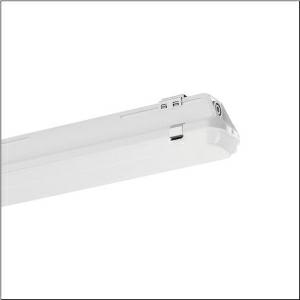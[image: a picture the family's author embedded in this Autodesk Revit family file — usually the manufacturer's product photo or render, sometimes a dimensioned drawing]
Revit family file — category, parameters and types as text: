
# Revit family: monsun_r__12_parking_51fg20dp440h_c783
name_source: partatom
category: Lighting Fixtures
units: mm (PartAtom-declared; Revit-internal decimal feet)

## family parameters
Cut with Voids When Loaded = No
Host = Face
Light Source = No
Part Type = Normal
Room Calculation Point = No
Round Connector Dimension = Use Diameter
Shared = No

## types (1)
- --- (1 x LED, 4840 lm, 30.8 W, 4000K)
    Apparent Load = 31 VA
    CIE Flux Codes = 45 75 93 94 100
    Color Rendering = 80
    Color Temperature = 4000K
    Default Elevation = 1800 mm
    Description = Monsun® 12 parking, damp-proof luminaire, chain hanger, primary optical cover: enclosure, of PC, light emission: direct distribution, primary light characteristic: symmetric, installation type: suspended mounting, surface-mounted, horizontal mounting, vertical mounting, LED rated luminous flux: 4.840 lm, light colour: 840, colour temperature: 4000K, control gear: ECG DALI, with terminal, 5-pole, max. 2.5mm², mains connection: 220..240V, AC, 50/60Hz, rated input power: 31W, luminaire housing, of glass-fibre reinforced polyester, uncoated, bright grey, length: 1.590 mm, width: 90 mm, height: 88mm, clip for enclosure, of stainless steel (V2A), ceiling mounting element, of stainless steel (V2A), chain hanger, of stainless steel (V2A), protection rating (complete): IP66, insulation class (complete): insulation class I (protective earthing), certification: CE, ENEC, VDE, protection symbol: D, impact resistance: IK08, permissible ambient temperature for indoor applications: -25..+40°C, standard: EN 50419, EN 60598-2-1, no direct snow, no direct sun, no direct rain, for indoor or canopied outdoor use, corresponds to IFS (International Featured Standards) requirements for safety and quality in the food industry, packaging unit: 1 piece
    Height = 89 mm
    Lamp = 1 x LED
    Lamp Light Flux = 4840 lm
    Lamp Power = 30.8 W
    Lamp count = 1
    Length = 1590 mm
    Luminous efficacy = 157 lm/W
    Manufacturer = Siteco
    ModVariant = No
    Model = 51FG20DP440H
    Mounting Place = Ceiling
    Mounting Type = Pendant
    Number of Poles = 1
    OnlyDefault = Yes
    Power Factor = 1
    Product Name = Monsun® 12 parking
    Product group = damp-proof luminaire | ceiling pendant
    ProductGroupID = 908
    Protection Class = Protection class I
    Protection Degree = IP 66
    RLX_Detail_Level = 1
    RlxData = <blob elided: 91789 chars, md5=4f84f886>
    Socket = socket
    Standby Power = 0 W
    System Light Flux = 4840 lm
    System Power = 31 W
    Type Comments = factory setting: luminous flux: 100 % | dim-lin: 254 | 205 mA
    Type Image = l_1004748.jpg
    URL = http://relux.com
    VarID = @adj_133735
    Voltage = 0 V
    Weight = 0.00 kg
    Width = 90 mm

## geometry (parser evidence)
native form markers: Blend x4, Sweep x15
no freeform markers — native parametric forms only
